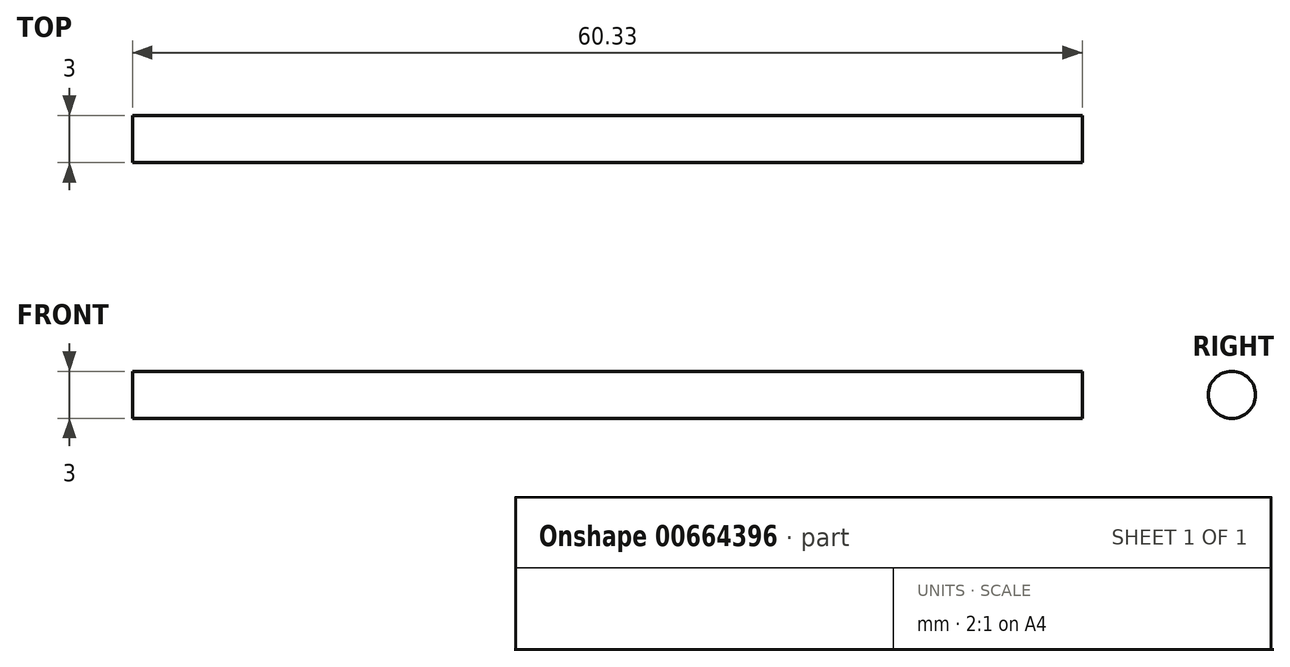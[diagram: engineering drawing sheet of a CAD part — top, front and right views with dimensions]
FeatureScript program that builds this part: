
annotation { "Feature Type Name" : "Feature", "Feature Type Description" : "" }
export const myFeature = defineFeature(function(context is Context, id is Id, definition is map)
    precondition{}
    {
        {
            var Q0;
            Q0=qCreatedBy(makeId("Right.planeOp"),FACE);
            var sketch = newSketch(context, id + "F0", { "sketchPlane" : qUnion([Q0])});
            skCircle(sketch, "E0", {"center": v(0, 0) * mm, "radius": 1.5 * mm});
            skSolve(sketch);
        }
        {
            var Q0;
            Q0=makeQuery(id+"F0.imprint","IMPRINT",FACE,{"disambiguationData":[TD([[makeQuery(id+"F0.imprint","IMPRINT",EDGE,{"derivedFrom":sQuery(id+"F0.wireOp",EDGE,"E0")}),1.0]])]});
            extrude(context, id + "F1", {"entities" : qUnion([Q0]), "depth" : 60.32 * mm, "offsetDistance" : 25.4 * mm});
        }
    });
